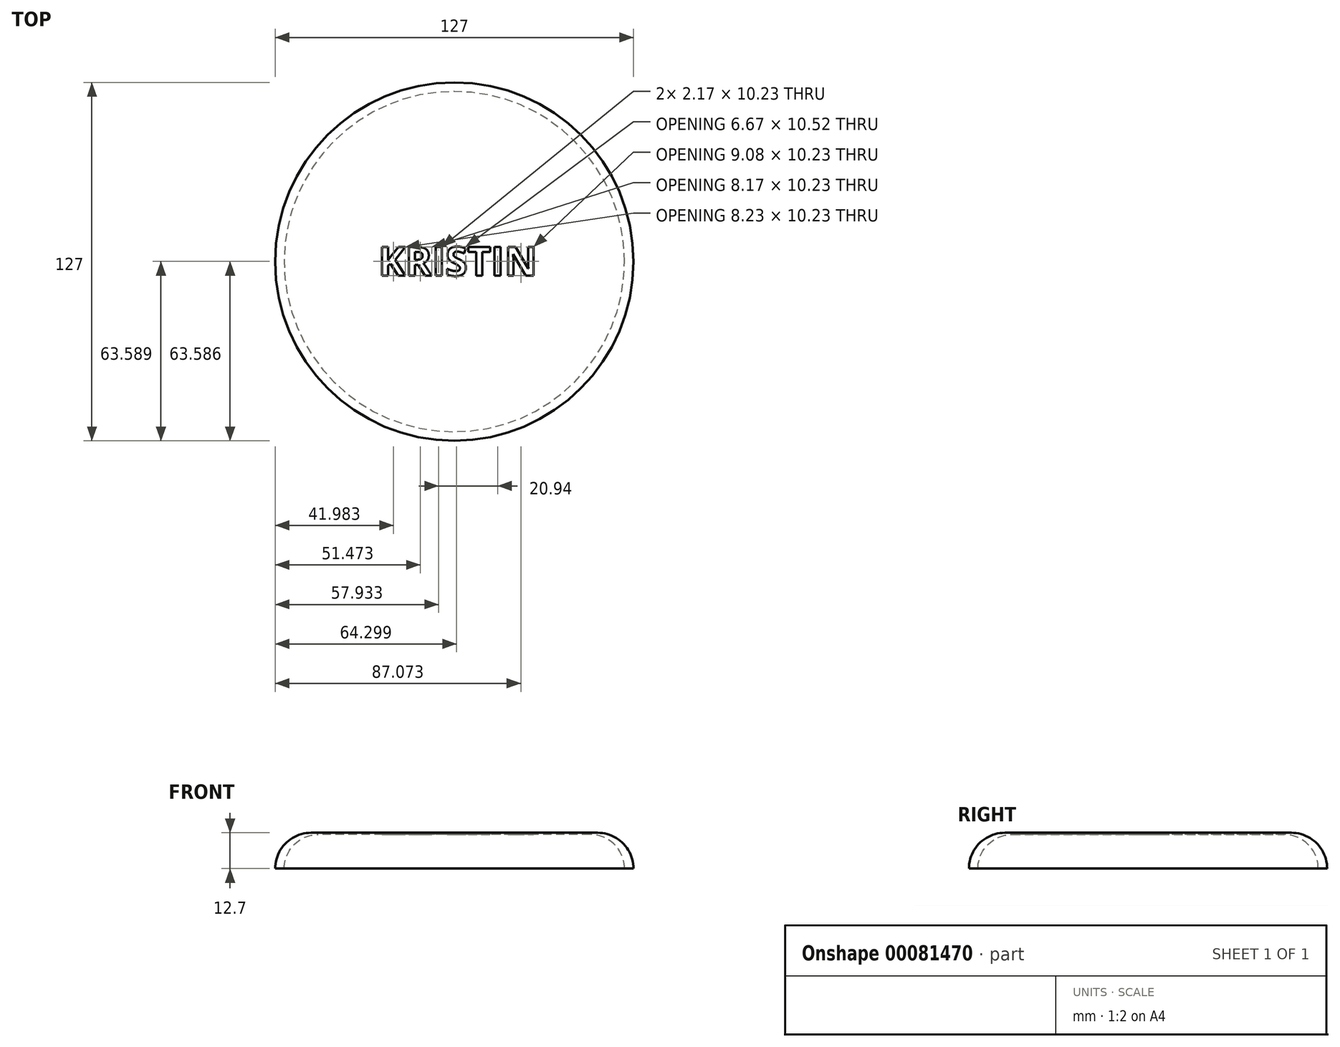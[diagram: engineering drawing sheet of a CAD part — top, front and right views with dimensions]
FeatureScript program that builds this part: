
annotation { "Feature Type Name" : "Feature", "Feature Type Description" : "" }
export const myFeature = defineFeature(function(context is Context, id is Id, definition is map)
    precondition{}
    {
        {
            var Q0;
            Q0=qCreatedBy(makeId("Top.planeOp"),FACE);
            var sketch = newSketch(context, id + "F0", { "sketchPlane" : qUnion([Q0])});
            skCircle(sketch, "E0", {"center": v(0, 0) * mm, "radius": 63.5 * mm});
            skSolve(sketch);
        }
        {
            var Q0;
            Q0 = qSketchRegion(id + "F0", true);
            extrude(context, id + "F1", {"entities" : qUnion([Q0]), "depth" : 12.7 * mm});
        }
        {
            var Q0;
            Q0=makeQuery(id+"F1.opExtrude","CAP_EDGE",EDGE,{"disambiguationData":[OSD([sQuery(id+"F0.wireOp",EDGE,"E0")])],"isStart":false});
            fillet(context, id + "F2", {"entities" : qUnion([Q0]), "radius" : 12.7 * mm, "tangentPropagation" : true, "allowEdgeOverflow" : false});
        }
        {
            var Q0;
            Q0=makeQuery(id+"F1.opExtrude","SWEPT_BODY",BODY,{"disambiguationData":[OSD([sQuery(id+"F0.wireOp",EDGE,"E0")])]});
            var Q1;
            Q1=qCreatedBy(makeId("Origin.pointOp"),VERTEX);
            transform(context, id + "F3", {"entities" : qUnion([Q0]), "transformType" : TransformType.SCALE_UNIFORMLY, "scale" : .95, "scalePoint" : qUnion([Q1]), "makeCopy" : true});
        }
        {
            var Q0;
            Q0=makeQuery(id+"F3.opPattern","COPY",BODY,{"derivedFrom":makeQuery(id+"F1.opExtrude","SWEPT_BODY",BODY,{"disambiguationData":[OSD([sQuery(id+"F0.wireOp",EDGE,"E0")])]}),"instanceName":"1"});
            var Q1;
            Q1=makeQuery(id+"F1.opExtrude","SWEPT_BODY",BODY,{"disambiguationData":[OSD([sQuery(id+"F0.wireOp",EDGE,"E0")])]});
            booleanBodies(context, id + "F4", {"operationType" : BooleanOperationType.SUBTRACTION, "tools" : qUnion([Q0]), "targets" : qUnion([Q1])});
        }
        {
            var Q0;
            Q0=makeQuery(id+"F1.opExtrude","CAP_FACE",FACE,{"disambiguationData":[OSD([sQuery(id+"F0.wireOp",EDGE,"E0")])],"isStart":false});
            var sketch = newSketch(context, id + "F5", { "sketchPlane" : qUnion([Q0])});
            skText(sketch, "E1", { "text": "KRISTIN", "fontName": "OpenSans-Bold.ttf"});
            const initialGuessF5  = {"E1": [-0.02692, -0.00503, 1, 0, 0.01032]};
            skSetInitialGuess(sketch, initialGuessF5);
            skSolve(sketch);
        }
        {
            var Q0;
            Q0 = qSketchRegion(id + "F5", true);
            extrude(context, id + "F6", {"entities" : qUnion([Q0]), "operationType" : NewBodyOperationType.REMOVE, "oppositeDirection" : true, "depth" : 12.7 * mm});
        }
    });
